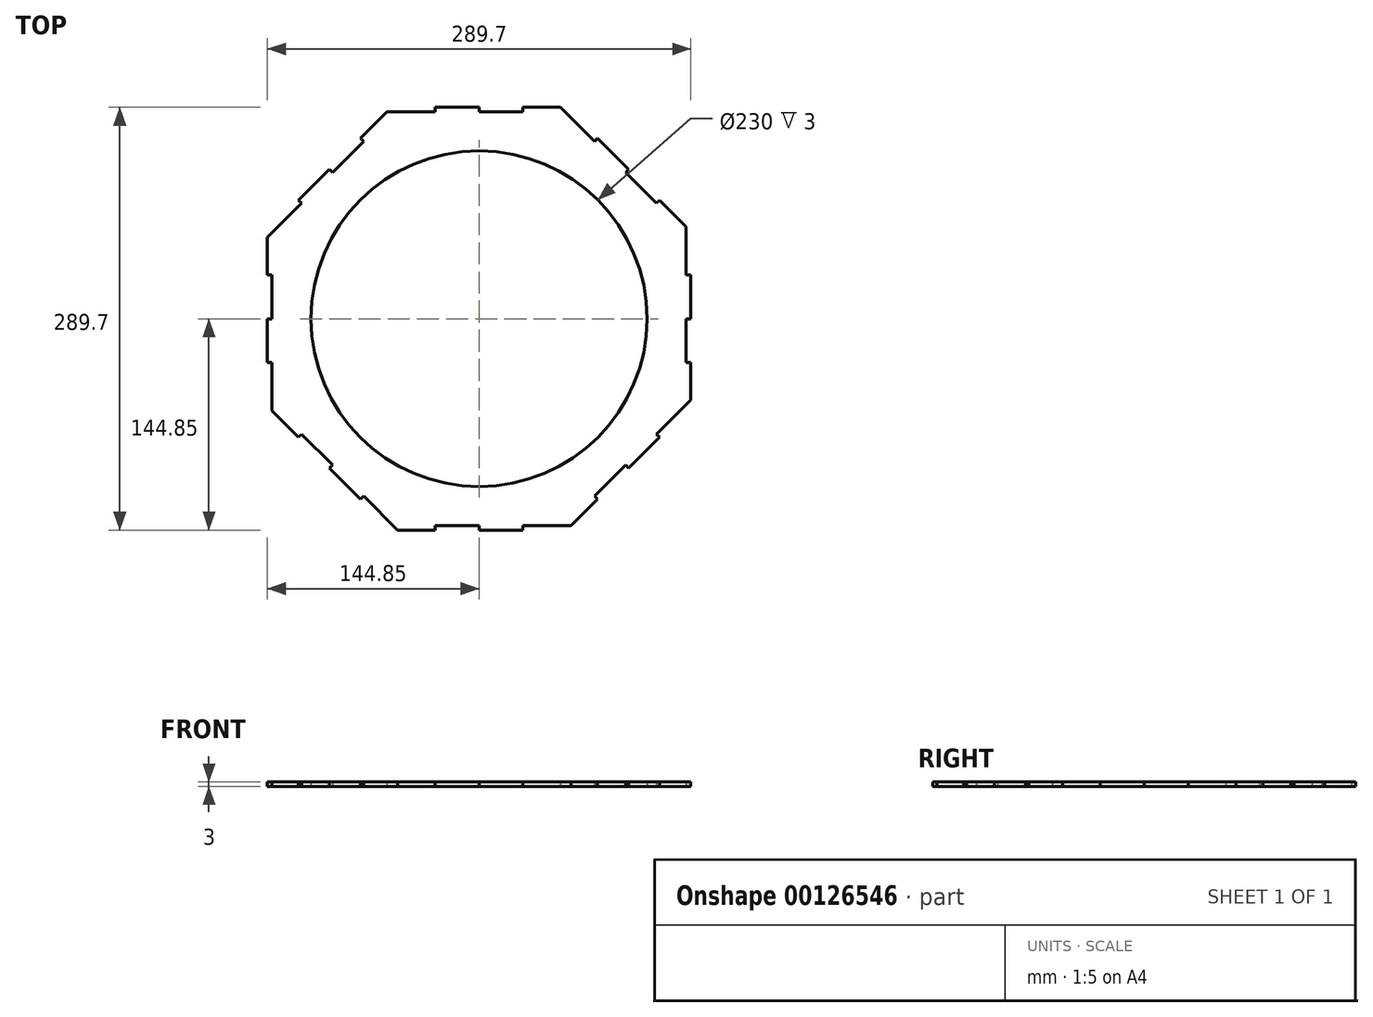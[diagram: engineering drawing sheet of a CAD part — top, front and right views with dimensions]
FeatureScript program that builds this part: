
annotation { "Feature Type Name" : "Feature", "Feature Type Description" : "" }
export const myFeature = defineFeature(function(context is Context, id is Id, definition is map)
    precondition{}
    {
        {
            var Q0;
            Q0=qCreatedBy(makeId("Top.planeOp"),FACE);
            var sketch = newSketch(context, id + "F0", { "sketchPlane" : qUnion([Q0])});
            skArc(sketch, "E0.cCircle", {"start": v(0, -144.85) * mm, "mid": v(14.74, 144.1) * mm, "end": v(-29.33, -141.85) * mm, "construction": true});
            skPoint(sketch, "E0.0.midPoint", {"position": v(0, 144.85) * mm});
            skLineSegment(sketch, "E1", {"start": v(0, 144.85) * mm, "end": v(0, -144.85) * mm, "construction": true});
            skLineSegment(sketch, "E2", {"start": v(144.85, 0) * mm, "end": v(-144.85, 0) * mm, "construction": true});
            skLineSegment(sketch, "E3", {"start": v(-144.85, 0) * mm, "end": v(-104.85, 0) * mm, "construction": true});
            skLineSegment(sketch, "E4", {"start": v(-55.76, -144.85) * mm, "end": v(-30, -144.85) * mm});
            skLineSegment(sketch, "E5", {"start": v(-30, -144.85) * mm, "end": v(-30, -141.85) * mm});
            skLineSegment(sketch, "E6", {"start": v(-30, -141.85) * mm, "end": v(0, -141.85) * mm});
            skLineSegment(sketch, "E7", {"start": v(0, -141.85) * mm, "end": v(0, -144.85) * mm});
            skLineSegment(sketch, "E8", {"start": v(0, -144.85) * mm, "end": v(30, -144.85) * mm});
            skLineSegment(sketch, "E9", {"start": v(30, -144.85) * mm, "end": v(30, -141.85) * mm});
            skLineSegment(sketch, "E10", {"start": v(60, -144.85) * mm, "end": v(0, -84.85) * mm, "construction": true});
            skLineSegment(sketch, "E11", {"start": v(0, -84.85) * mm, "end": v(-60, -144.85) * mm, "construction": true});
            skLineSegment(sketch, "E12", {"start": v(30, -141.85) * mm, "end": v(57, -141.85) * mm});
            skLineSegment(sketch, "E13.trimOffspring", {"start": v(-30, -144.85) * mm, "end": v(-55.76, -144.85) * mm});
            skLineSegment(sketch, "E14.trimOffspring", {"start": v(30, -144.85) * mm, "end": v(0, -144.85) * mm});
            skLineSegment(sketch, "E15", {"start": v(63, -141.85) * mm, "end": v(81.21, -123.64) * mm});
            skLineSegment(sketch, "E16", {"start": v(81.21, -123.64) * mm, "end": v(79.1, -121.52) * mm});
            skLineSegment(sketch, "E17", {"start": v(79.1, -121.52) * mm, "end": v(100.3, -100.3) * mm});
            skLineSegment(sketch, "E18", {"start": v(100.3, -100.3) * mm, "end": v(102.43, -102.42) * mm});
            skLineSegment(sketch, "E19", {"start": v(102.43, -102.42) * mm, "end": v(123.64, -81.21) * mm});
            skLineSegment(sketch, "E20", {"start": v(123.64, -81.21) * mm, "end": v(121.52, -79.09) * mm});
            skLineSegment(sketch, "E21", {"start": v(121.52, -79.09) * mm, "end": v(140.6, -60) * mm});
            skLineSegment(sketch, "E22", {"start": v(144.85, -55.76) * mm, "end": v(144.85, -30) * mm});
            skLineSegment(sketch, "E23", {"start": v(144.85, -30) * mm, "end": v(141.85, -30) * mm});
            skLineSegment(sketch, "E24", {"start": v(141.85, -30) * mm, "end": v(141.85, 0) * mm});
            skLineSegment(sketch, "E25", {"start": v(141.85, 0) * mm, "end": v(144.85, 0) * mm});
            skLineSegment(sketch, "E26", {"start": v(144.85, 0) * mm, "end": v(144.85, 30) * mm});
            skLineSegment(sketch, "E27", {"start": v(144.85, 30) * mm, "end": v(141.85, 30) * mm});
            skLineSegment(sketch, "E28", {"start": v(141.85, 30) * mm, "end": v(141.85, 57) * mm});
            skLineSegment(sketch, "E29", {"start": v(141.85, 63) * mm, "end": v(123.64, 81.21) * mm});
            skLineSegment(sketch, "E30", {"start": v(123.64, 81.21) * mm, "end": v(121.52, 79.1) * mm});
            skLineSegment(sketch, "E31", {"start": v(121.52, 79.1) * mm, "end": v(100.3, 100.3) * mm});
            skLineSegment(sketch, "E32", {"start": v(100.3, 100.3) * mm, "end": v(102.42, 102.43) * mm});
            skLineSegment(sketch, "E33", {"start": v(102.42, 102.43) * mm, "end": v(81.21, 123.64) * mm});
            skLineSegment(sketch, "E34", {"start": v(81.21, 123.64) * mm, "end": v(79.09, 121.52) * mm});
            skLineSegment(sketch, "E35", {"start": v(79.09, 121.52) * mm, "end": v(60, 140.6) * mm});
            skLineSegment(sketch, "E36", {"start": v(55.76, 144.85) * mm, "end": v(30, 144.85) * mm});
            skLineSegment(sketch, "E37", {"start": v(30, 144.85) * mm, "end": v(30, 141.85) * mm});
            skLineSegment(sketch, "E38", {"start": v(30, 141.85) * mm, "end": v(0, 141.85) * mm});
            skLineSegment(sketch, "E39", {"start": v(0, 141.85) * mm, "end": v(0, 144.85) * mm});
            skLineSegment(sketch, "E40", {"start": v(0, 144.85) * mm, "end": v(-30, 144.85) * mm});
            skLineSegment(sketch, "E41", {"start": v(-30, 144.85) * mm, "end": v(-30, 141.85) * mm});
            skLineSegment(sketch, "E42", {"start": v(-30, 141.85) * mm, "end": v(-57, 141.85) * mm});
            skLineSegment(sketch, "E43", {"start": v(-63, 141.85) * mm, "end": v(-81.21, 123.64) * mm});
            skLineSegment(sketch, "E44", {"start": v(-81.21, 123.64) * mm, "end": v(-79.1, 121.52) * mm});
            skLineSegment(sketch, "E45", {"start": v(-79.1, 121.52) * mm, "end": v(-100.3, 100.3) * mm});
            skLineSegment(sketch, "E46", {"start": v(-100.3, 100.3) * mm, "end": v(-102.43, 102.42) * mm});
            skLineSegment(sketch, "E47", {"start": v(-102.43, 102.42) * mm, "end": v(-123.64, 81.21) * mm});
            skLineSegment(sketch, "E48", {"start": v(-123.64, 81.21) * mm, "end": v(-121.52, 79.09) * mm});
            skLineSegment(sketch, "E49", {"start": v(-121.52, 79.09) * mm, "end": v(-140.6, 60) * mm});
            skLineSegment(sketch, "E50", {"start": v(-144.85, 55.76) * mm, "end": v(-144.85, 30) * mm});
            skLineSegment(sketch, "E51", {"start": v(-144.85, 30) * mm, "end": v(-141.85, 30) * mm});
            skLineSegment(sketch, "E52", {"start": v(-141.85, 30) * mm, "end": v(-141.85, 0) * mm});
            skLineSegment(sketch, "E53", {"start": v(-141.85, 0) * mm, "end": v(-144.85, 0) * mm});
            skLineSegment(sketch, "E54", {"start": v(-144.85, 0) * mm, "end": v(-144.85, -30) * mm});
            skLineSegment(sketch, "E55", {"start": v(-144.85, -30) * mm, "end": v(-141.85, -30) * mm});
            skLineSegment(sketch, "E56", {"start": v(-141.85, -30) * mm, "end": v(-141.85, -57) * mm});
            skLineSegment(sketch, "E57", {"start": v(-141.85, -63) * mm, "end": v(-123.64, -81.21) * mm});
            skLineSegment(sketch, "E58", {"start": v(-123.64, -81.21) * mm, "end": v(-121.52, -79.1) * mm});
            skLineSegment(sketch, "E59", {"start": v(-121.52, -79.1) * mm, "end": v(-100.3, -100.3) * mm});
            skLineSegment(sketch, "E60", {"start": v(-100.3, -100.3) * mm, "end": v(-102.42, -102.43) * mm});
            skLineSegment(sketch, "E61", {"start": v(-102.42, -102.43) * mm, "end": v(-81.21, -123.64) * mm});
            skLineSegment(sketch, "E62", {"start": v(-81.21, -123.64) * mm, "end": v(-79.09, -121.52) * mm});
            skLineSegment(sketch, "E63", {"start": v(-79.09, -121.52) * mm, "end": v(-60, -140.6) * mm});
            skLineSegment(sketch, "E64.trimOffspring", {"start": v(-81.21, -123.64) * mm, "end": v(-102.42, -102.42) * mm});
            skLineSegment(sketch, "E65.trimOffspring", {"start": v(-123.64, -81.21) * mm, "end": v(-141.85, -63) * mm});
            skLineSegment(sketch, "E66.trimOffspring", {"start": v(-144.85, -30) * mm, "end": v(-144.85, 0) * mm});
            skLineSegment(sketch, "E67.trimOffspring", {"start": v(-144.85, 30) * mm, "end": v(-144.85, 55.76) * mm});
            skLineSegment(sketch, "E68.trimOffspring", {"start": v(-123.64, 81.21) * mm, "end": v(-102.42, 102.42) * mm});
            skLineSegment(sketch, "E69.trimOffspring", {"start": v(-81.21, 123.64) * mm, "end": v(-63, 141.85) * mm});
            skLineSegment(sketch, "E70.trimOffspring", {"start": v(-30, 144.85) * mm, "end": v(0, 144.85) * mm});
            skLineSegment(sketch, "E71.trimOffspring", {"start": v(30, 144.85) * mm, "end": v(55.76, 144.85) * mm});
            skLineSegment(sketch, "E72", {"start": v(0, 144.85) * mm, "end": v(30, 144.85) * mm, "construction": true});
            skLineSegment(sketch, "E73.trimOffspring", {"start": v(81.21, 123.64) * mm, "end": v(102.42, 102.42) * mm});
            skLineSegment(sketch, "E74.trimOffspring", {"start": v(123.64, 81.21) * mm, "end": v(141.85, 63) * mm});
            skLineSegment(sketch, "E75", {"start": v(102.42, 102.42) * mm, "end": v(123.64, 81.21) * mm, "construction": true});
            skLineSegment(sketch, "E76.trimOffspring", {"start": v(81.21, -123.64) * mm, "end": v(63, -141.85) * mm});
            skLineSegment(sketch, "E77.trimOffspring", {"start": v(123.64, -81.21) * mm, "end": v(102.42, -102.42) * mm});
            skLineSegment(sketch, "E78.trimOffspring", {"start": v(144.85, -30) * mm, "end": v(144.85, -55.76) * mm});
            skLineSegment(sketch, "E79.trimOffspring", {"start": v(144.85, 30) * mm, "end": v(144.85, 0) * mm});
            skLineSegment(sketch, "E80", {"start": v(144.85, -30) * mm, "end": v(144.85, 0) * mm, "construction": true});
            skLineSegment(sketch, "E81", {"start": v(144.85, 30) * mm, "end": v(144.85, 57) * mm, "construction": true});
            skCircle(sketch, "E82", {"center": v(0, 0) * mm, "radius": 115 * mm});
            skLineSegment(sketch, "E83", {"start": v(-57, 141.85) * mm, "end": v(-63, 141.85) * mm});
            skLineSegment(sketch, "E84", {"start": v(60, 140.6) * mm, "end": v(55.76, 144.85) * mm});
            skLineSegment(sketch, "E85", {"start": v(141.85, 57) * mm, "end": v(141.85, 63) * mm});
            skLineSegment(sketch, "E86", {"start": v(140.6, -60) * mm, "end": v(144.85, -55.76) * mm});
            skLineSegment(sketch, "E87", {"start": v(-140.6, 60) * mm, "end": v(-144.85, 55.76) * mm});
            skLineSegment(sketch, "E88", {"start": v(-141.85, -57) * mm, "end": v(-141.85, -63) * mm});
            skLineSegment(sketch, "E89", {"start": v(-60, -140.6) * mm, "end": v(-55.76, -144.85) * mm});
            skLineSegment(sketch, "E90", {"start": v(57, -141.85) * mm, "end": v(63, -141.85) * mm});
            skSolve(sketch);
        }
        {
            var Q0;
            Q0=qSketchRegion(id+"F0",true);
            var Q1;
            Q1=qConstructionFilter(qBodyType(qCreatedBy(id+"F0",EDGE),BodyType.WIRE),ConstructionObject.NO);
            extrude(context, id + "F1", {"entities" : qUnion([Q0]), "surfaceEntities" : qUnion([Q1]), "endBound" : BoundingType.SYMMETRIC, "depth" : 3 * mm});
        }
    });
